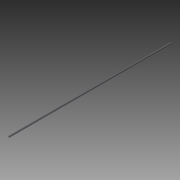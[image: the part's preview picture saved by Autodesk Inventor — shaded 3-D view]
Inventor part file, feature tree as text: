
AUTODESK INVENTOR PART (.ipt)
format: ipt  version: 2015 SP2 (Build 190223200, 223)  size: 71,168 bytes
history: native  units: mm
features: extrude x1, thread x1, sketch x1
ambient origin geometry x8: Origin, YZ Plane, XZ Plane, XY Plane, X Axis, Y Axis, Z Axis, Center Point
bodies: Solid1 (feature_tree)
feature tree (3):
  extrude  "Extrusion1"  Depth=10.0mm TaperAngle=0.0deg
  thread  "Thread1"  [1 undecoded]
  sketch  "Sketch1"  dims[d1=400.0mm d2=0.0mm d3=10.0mm d4=0.0mm]
note: 1 required parameter value undecoded (feature->parameter linkage not recoverable at this tier; creation-order binding heuristic only, values carry confidence <= 0.55)
